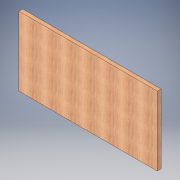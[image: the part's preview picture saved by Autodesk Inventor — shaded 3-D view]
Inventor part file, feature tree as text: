
AUTODESK INVENTOR PART (.ipt)
format: ipt  version: 2017 (Build 210142000, 142)  size: 112,640 bytes
history: native  units: in
note: dims shown in document units (in); Inventor stores cm internally (conversion verified against a paired STEP export)
features: extrude x1, sketch x1
ambient origin geometry x8: Origin, YZ Plane, XZ Plane, XY Plane, X Axis, Y Axis, Z Axis, Center Point
bodies: Body1 (feature_tree)
feature tree (2):
  extrude  "Extrusion2"  Depth=2.0in
  sketch  "Sketch2"  dims[d4=72.0in d5=2.0in d6=36.0in d7=0.0in]
